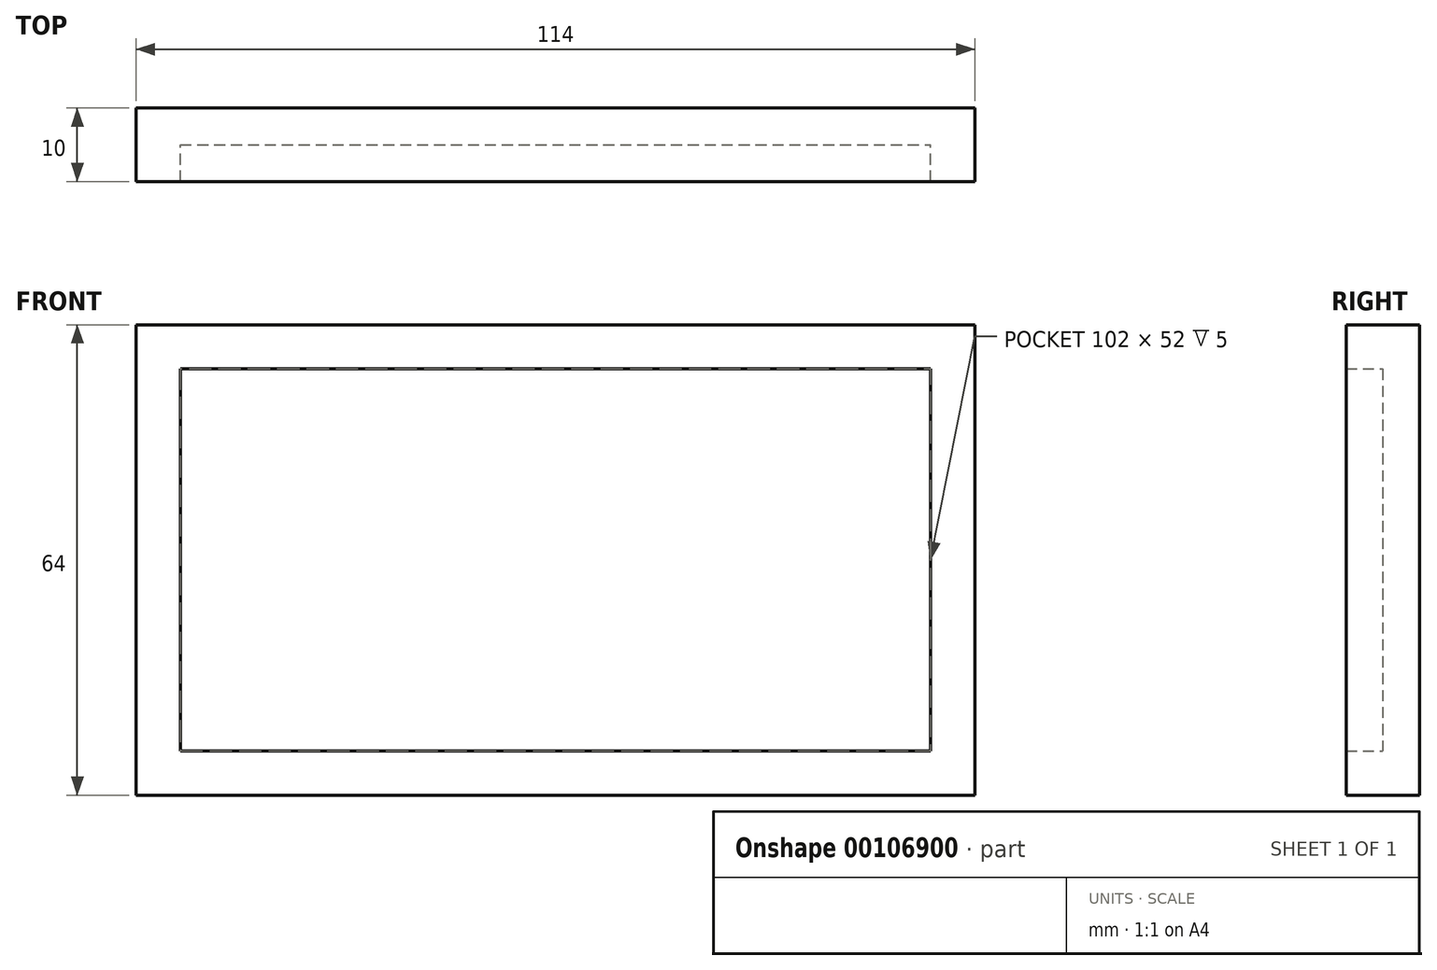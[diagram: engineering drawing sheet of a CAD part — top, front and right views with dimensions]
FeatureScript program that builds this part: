
annotation { "Feature Type Name" : "Feature", "Feature Type Description" : "" }
export const myFeature = defineFeature(function(context is Context, id is Id, definition is map)
    precondition{}
    {
        {
            var Q0;
            Q0=qCreatedBy(makeId("Front.planeOp"),FACE);
            var sketch = newSketch(context, id + "F0", { "sketchPlane" : qUnion([Q0])});
            skLineSegment(sketch, "E0.bottom", {"start": v(-57, 32) * mm, "end": v(57, 32) * mm});
            skLineSegment(sketch, "E0.top", {"start": v(-57, -32) * mm, "end": v(57, -32) * mm});
            skLineSegment(sketch, "E0.left", {"start": v(-57, 32) * mm, "end": v(-57, -32) * mm});
            skLineSegment(sketch, "E0.right", {"start": v(57, 32) * mm, "end": v(57, -32) * mm});
            skPoint(sketch, "E0.middle", {"position": v(0, 0) * mm});
            skSolve(sketch);
        }
        {
            var Q0;
            Q0 = qSketchRegion(id + "F0", true);
            extrude(context, id + "F1", {"entities" : qUnion([Q0]), "depth" : 5 * mm});
        }
        {
            var Q0;
            Q0=makeQuery(id+"F1.opExtrude","CAP_FACE",FACE,{"disambiguationData":[OSD([sQuery(id+"F0.wireOp",EDGE,"E0.bottom"),sQuery(id+"F0.wireOp",EDGE,"E0.top"),sQuery(id+"F0.wireOp",EDGE,"E0.left"),sQuery(id+"F0.wireOp",EDGE,"E0.right")])],"isStart":false});
            var sketch = newSketch(context, id + "F2", { "sketchPlane" : qUnion([Q0])});
            skLineSegment(sketch, "E1.bottom", {"start": v(-51, 26) * mm, "end": v(51, 26) * mm});
            skLineSegment(sketch, "E1.top", {"start": v(-51, -26) * mm, "end": v(51, -26) * mm});
            skLineSegment(sketch, "E1.left", {"start": v(-51, 26) * mm, "end": v(-51, -26) * mm});
            skLineSegment(sketch, "E1.right", {"start": v(51, 26) * mm, "end": v(51, -26) * mm});
            skPoint(sketch, "E1.middle", {"position": v(0, 0) * mm});
            skSolve(sketch);
        }
        {
            var Q0;
            Q0=makeQuery(id+"F2.imprint","IMPRINT",FACE,{"disambiguationData":[TD([[makeQuery(id+"F2.imprint","IMPRINT",EDGE,{"derivedFrom":sQuery(id+"F2.wireOp",EDGE,"E1.bottom")}),1.0]])]});
            extrude(context, id + "F3", {"entities" : qUnion([Q0]), "operationType" : NewBodyOperationType.ADD, "depth" : 5 * mm});
        }
    });
